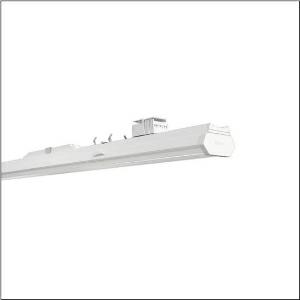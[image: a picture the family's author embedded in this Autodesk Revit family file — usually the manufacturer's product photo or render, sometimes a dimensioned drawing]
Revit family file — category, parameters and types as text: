
# Revit family: licross_11_protected_mo_51td12dn495g3c
name_source: partatom
category: Lighting Fixtures
units: mm (PartAtom-declared; Revit-internal decimal feet)

## family parameters
Cut with Voids When Loaded = No
Host = Face
Light Source = No
Part Type = Normal
Room Calculation Point = No
Round Connector Dimension = Use Diameter
Shared = No

## types (1)
- --- (1 x LED, 980 lm, 6.8 W, 4000K)
    Apparent Load = 7 VA
    CIE Flux Codes = 73 92 98 99 100
    Color Rendering = 80
    Color Temperature = 4000K
    Default Elevation = 1800 mm
    Description = Licross 11 Protected MO, luminaire insert, of sheet steel, galvanised, coil coated, white, length: 1.500mm, width: 90mm, height: 101mm, LED rated luminous flux: 9.980lm, light colour: 840, SDCM (Standard Deviation of Colour Matching)MacAdam ≤ 2 SDCM (initial), control gear: DALI 2 (for two DALI lines), with plug, 6-pole, with phase selection, for trunking rail, 14-core, mains connection: 220..240V, AC, 50/60Hz, rated input power: 61W, for trunking rail, 14-core, internal wiring halogen-free, for emergency light function, converter,control gear: single battery element, battery: LiFePO4, 9Ah, primary light control with lens, of plastic, primary optical cover: cover, of PMMA, light emission: direct distribution, primary light characteristic: symmetric, protection rating (complete): IP54, insulation class (complete): insulation class I (protective earthing), certification: CE, UKCA, protection symbol: D if used in an environment with non-conductive dust loads with corresponding accessories, impact resistance: IK06, permissible ambient temperature for indoor applications: +5..+35°C, standard: EN 60598-2-22, LABS conformity tested according to VDMA 24364:2018-05, reducing of maximum allowable ambient temperature of 5°C with ceiling mounting, corresponds to IFS (International Featured Standards) requirements for safety and quality in the food industry, The light source and the operating device comply with the requirements of the Ecodesign Regulation (EU) 2019/2020 and are replaceable in accordance with this regulation, packaging unit: 1 piece
    Height = 92 mm
    Lamp = 1 x LED
    Lamp Light Flux = 980 lm
    Lamp Power = 6.8 W
    Lamp count = 1
    Length = 1500 mm
    Luminous efficacy = 144 lm/W
    Manufacturer = Siteco
    ModVariant = No
    Model = 51TD12DN495G3C
    Mounting Place = Ceiling
    Mounting Type = Pendant
    Number of Poles = 1
    OnlyDefault = Yes
    Power Factor = 1
    Product Name = Licross 11 Protected MO
    Product group = luminaire insert | ceiling pendant
    ProductGroupID = 901
    Protection Class = Protection class I
    Protection Degree = IP 54
    RLX_Detail_Level = 1
    RLX_Emergency_Light_Flux = 0 lm
    RLX_Emergency_Type = 0
    RLX_Emergency_Type_DB = No
    RlxData = <blob elided: 25069 chars, md5=f3c7367c>
    Socket = socket
    Standby Power = 0 W
    System Light Flux = 980 lm
    System Power = 7 W
    Type Comments = : emergency light operation: 3 h
    Type Image = l_1256145.jpg
    URL = http://relux.com
    VarID = @adj_094525
    Voltage = 0 V
    Weight = 0.00 kg
    Width = 88 mm

## geometry (parser evidence)
native form markers: Blend x4, Sweep x8
no freeform markers — native parametric forms only
